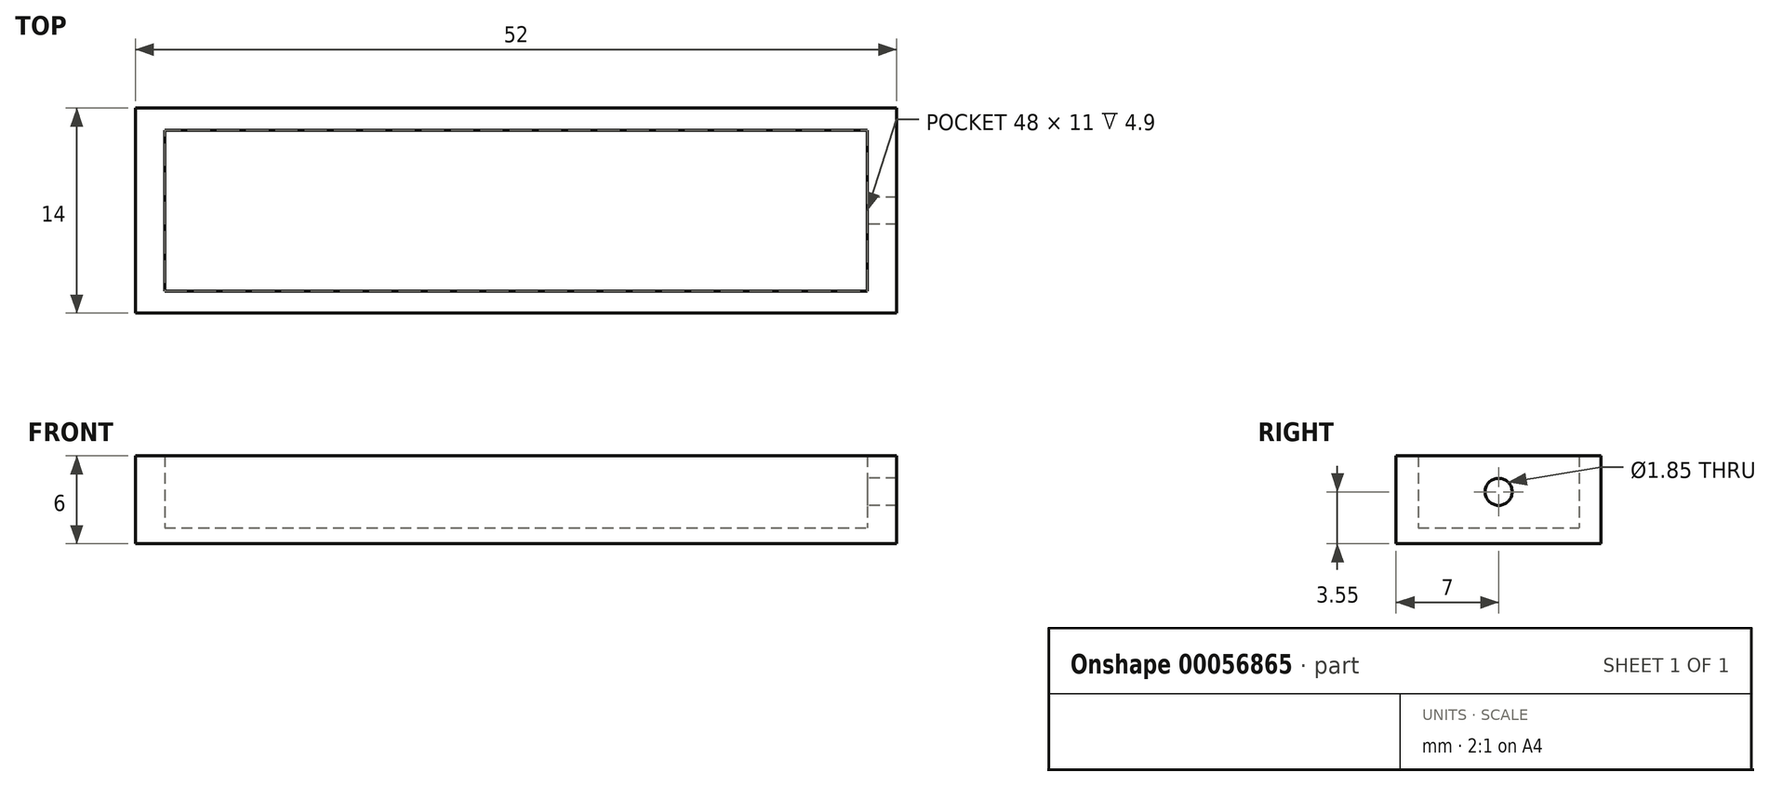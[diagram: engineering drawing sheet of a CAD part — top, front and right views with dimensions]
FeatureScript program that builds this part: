
annotation { "Feature Type Name" : "Feature", "Feature Type Description" : "" }
export const myFeature = defineFeature(function(context is Context, id is Id, definition is map)
    precondition{}
    {
        {
            var Q0;
            Q0=qCreatedBy(makeId("Top.planeOp"),FACE);
            var sketch = newSketch(context, id + "F0", { "sketchPlane" : qUnion([Q0])});
            skLineSegment(sketch, "E0", {"start": v(0, 7) * mm, "end": v(0, -7) * mm, "construction": true});
            skLineSegment(sketch, "E1.0", {"start": v(-24, 7) * mm, "end": v(-24, -7) * mm, "construction": true});
            skLineSegment(sketch, "E2.0", {"start": v(24, 7) * mm, "end": v(24, -7) * mm, "construction": true});
            skLineSegment(sketch, "E3", {"start": v(-27.72, 0) * mm, "end": v(24, 0) * mm, "construction": true});
            skLineSegment(sketch, "E4.0", {"start": v(-26, -7) * mm, "end": v(27.82, -7) * mm, "construction": true});
            skLineSegment(sketch, "E5.0", {"start": v(-26, 7) * mm, "end": v(27.82, 7) * mm, "construction": true});
            skLineSegment(sketch, "E6.0", {"start": v(-26, -5.5) * mm, "end": v(24, -5.5) * mm, "construction": true});
            skLineSegment(sketch, "E7.0", {"start": v(-26, 5.5) * mm, "end": v(24, 5.5) * mm, "construction": true});
            skLineSegment(sketch, "E8.0", {"start": v(26, 7) * mm, "end": v(26, -7) * mm, "construction": true});
            skLineSegment(sketch, "E9.0", {"start": v(-26, 7) * mm, "end": v(-26, -7) * mm, "construction": true});
            skPoint(sketch, "E10.orphan", {"position": v(0, 12.03) * mm});
            skLineSegment(sketch, "E11", {"start": v(-26, 7) * mm, "end": v(26, 7) * mm});
            skLineSegment(sketch, "E12", {"start": v(26, -7) * mm, "end": v(-26, -7) * mm});
            skLineSegment(sketch, "E13", {"start": v(-26, -7) * mm, "end": v(-26, 7) * mm});
            skLineSegment(sketch, "E14", {"start": v(26, 7) * mm, "end": v(26, -7) * mm});
            skLineSegment(sketch, "E15", {"start": v(24, -5.5) * mm, "end": v(24, 5.5) * mm});
            skLineSegment(sketch, "E16", {"start": v(24, 5.5) * mm, "end": v(-24, 5.5) * mm});
            skLineSegment(sketch, "E17", {"start": v(-24, 5.5) * mm, "end": v(-24, -5.5) * mm});
            skLineSegment(sketch, "E18", {"start": v(-24, -5.5) * mm, "end": v(24, -5.5) * mm});
            skLineSegment(sketch, "E19.trimOffspring", {"start": v(26, -5.5) * mm, "end": v(27.82, -5.5) * mm, "construction": true});
            skLineSegment(sketch, "E20.trimOffspring", {"start": v(26, 0) * mm, "end": v(27.82, 0) * mm, "construction": true});
            skLineSegment(sketch, "E21.trimOffspring", {"start": v(26, 5.5) * mm, "end": v(27.82, 5.5) * mm, "construction": true});
            skSolve(sketch);
        }
        {
            var Q0;
            Q0=makeQuery(id+"F0.imprint","IMPRINT",FACE,{"disambiguationData":[TD([[makeQuery(id+"F0.imprint","IMPRINT",EDGE,{"derivedFrom":sQuery(id+"F0.wireOp",EDGE,"E15")}),1.0]])]});
            extrude(context, id + "F1", {"entities" : qUnion([Q0]), "depth" : 1.1 * mm});
        }
        {
            var Q0;
            Q0=makeQuery(id+"F0.imprint","IMPRINT",FACE,{"disambiguationData":[TD([[makeQuery(id+"F0.imprint","IMPRINT",EDGE,{"derivedFrom":sQuery(id+"F0.wireOp",EDGE,"E11")}),-1.0]])]});
            extrude(context, id + "F2", {"entities" : qUnion([Q0]), "operationType" : NewBodyOperationType.ADD, "depth" : 6 * mm});
        }
        {
            var Q0;
            Q0=makeQuery(id+"F2.opExtrude","SWEPT_FACE",FACE,{"disambiguationData":[OSD([sQuery(id+"F0.wireOp",EDGE,"E15")])]});
            var sketch = newSketch(context, id + "F3", { "sketchPlane" : qUnion([Q0])});
            skCircle(sketch, "E22", {"center": v(0, 3.55) * mm, "radius": 0.93 * mm});
            skPoint(sketch, "E22.centerSnap0", {"position": v(5.5, 3.55) * mm});
            skPoint(sketch, "E22.centerSnap1", {"position": v(0, 6) * mm});
            skSolve(sketch);
        }
        {
            var Q0;
            Q0=makeQuery(id+"F3.imprint","IMPRINT",FACE,{"disambiguationData":[TD([[makeQuery(id+"F3.imprint","IMPRINT",EDGE,{"derivedFrom":sQuery(id+"F3.wireOp",EDGE,"E22")}),1.0]])]});
            extrude(context, id + "F4", {"entities" : qUnion([Q0]), "operationType" : NewBodyOperationType.REMOVE, "oppositeDirection" : true, "depth" : 25 * mm});
        }
    });
